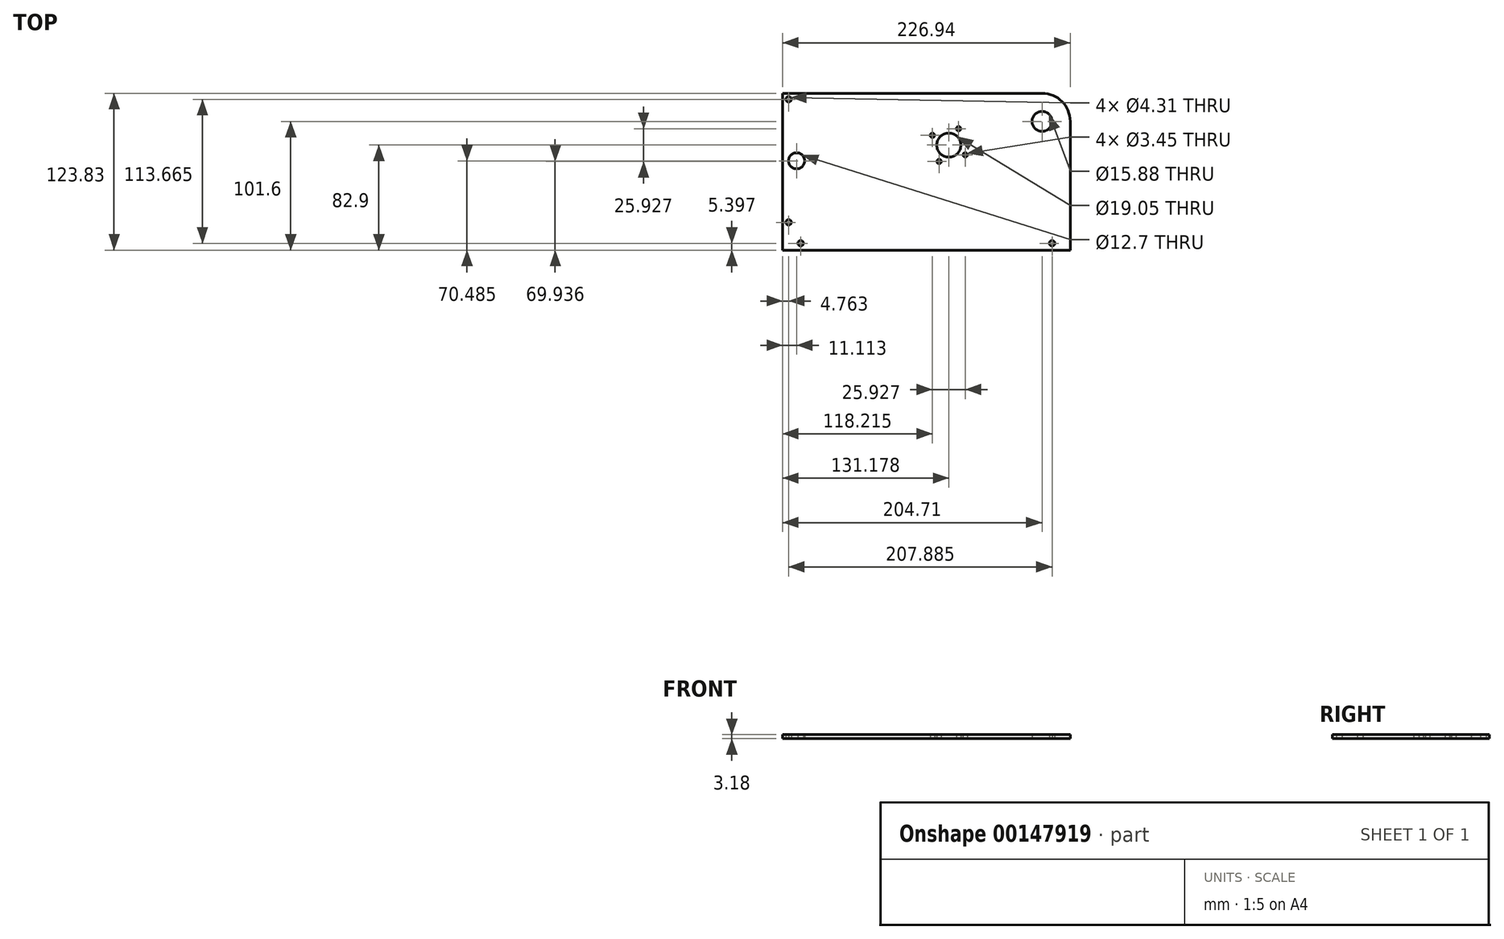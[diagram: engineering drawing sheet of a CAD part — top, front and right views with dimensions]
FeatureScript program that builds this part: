
annotation { "Feature Type Name" : "Feature", "Feature Type Description" : "" }
export const myFeature = defineFeature(function(context is Context, id is Id, definition is map)
    precondition{}
    {
        {
            var Q0;
            Q0=qCreatedBy(makeId("Top.planeOp"),FACE);
            var sketch = newSketch(context, id + "F0", { "sketchPlane" : qUnion([Q0])});
            skCircle(sketch, "E0", {"center": v(0, 0) * mm, "radius": 7.94 * mm});
            skLineSegment(sketch, "E1.bottom", {"start": v(-204.7, 22.22) * mm, "end": v(0, 22.23) * mm});
            skLineSegment(sketch, "E1.top", {"start": v(-204.7, -101.6) * mm, "end": v(22.23, -101.6) * mm});
            skLineSegment(sketch, "E1.left", {"start": v(-204.7, 22.22) * mm, "end": v(-204.7, -101.6) * mm});
            skArc(sketch, "E2", {"start": v(22.23, 0) * mm, "mid": v(15.72, 15.72) * mm, "end": v(0, 22.23) * mm});
            skLineSegment(sketch, "E3", {"start": v(22.23, -101.6) * mm, "end": v(22.23, -90.8) * mm});
            skLineSegment(sketch, "E4", {"start": v(22.23, -90.8) * mm, "end": v(22.23, 0) * mm});
            skLineSegment(sketch, "E5", {"start": v(0, 0) * mm, "end": v(0, -101.6) * mm, "construction": true});
            skLineSegment(sketch, "E6", {"start": v(22.23, -96.2) * mm, "end": v(7.94, -96.2) * mm, "construction": true});
            skCircle(sketch, "E7", {"center": v(7.94, -96.2) * mm, "radius": 2.15 * mm});
            skLineSegment(sketch, "E8", {"start": v(-199.95, 22.22) * mm, "end": v(-199.95, 17.46) * mm, "construction": true});
            skLineSegment(sketch, "E9", {"start": v(-204.7, -96.2) * mm, "end": v(-190.42, -96.2) * mm, "construction": true});
            skCircle(sketch, "E10", {"center": v(-190.42, -96.2) * mm, "radius": 2.15 * mm});
            skCircle(sketch, "E11", {"center": v(-199.95, 17.46) * mm, "radius": 2.15 * mm});
            skLineSegment(sketch, "E12", {"start": v(-199.95, -79.7) * mm, "end": v(-199.95, 17.46) * mm, "construction": true});
            skLineSegment(sketch, "E13", {"start": v(-199.95, -79.7) * mm, "end": v(-199.95, -96.2) * mm, "construction": true});
            skCircle(sketch, "E14", {"center": v(-199.95, -79.7) * mm, "radius": 2.15 * mm});
            skLineSegment(sketch, "E15", {"start": v(0, 0) * mm, "end": v(-73.53, -18.7) * mm, "construction": true});
            skLineSegment(sketch, "E16.bottom", {"start": v(-86.5, -11) * mm, "end": v(-65.83, -5.74) * mm, "construction": true});
            skLineSegment(sketch, "E16.top", {"start": v(-81.24, -31.66) * mm, "end": v(-60.57, -26.4) * mm, "construction": true});
            skLineSegment(sketch, "E16.left", {"start": v(-86.5, -11) * mm, "end": v(-81.24, -31.66) * mm, "construction": true});
            skLineSegment(sketch, "E16.right", {"start": v(-65.83, -5.74) * mm, "end": v(-60.57, -26.4) * mm, "construction": true});
            skPoint(sketch, "E16.middle", {"position": v(-73.53, -18.7) * mm});
            skCircle(sketch, "E17", {"center": v(-86.5, -11) * mm, "radius": 1.73 * mm});
            skCircle(sketch, "E18", {"center": v(-65.83, -5.74) * mm, "radius": 1.73 * mm});
            skCircle(sketch, "E19", {"center": v(-73.53, -18.7) * mm, "radius": 9.53 * mm});
            skCircle(sketch, "E20", {"center": v(-81.24, -31.66) * mm, "radius": 1.73 * mm});
            skCircle(sketch, "E21", {"center": v(-60.57, -26.4) * mm, "radius": 1.73 * mm});
            skCircle(sketch, "E22", {"center": v(-73.53, -18.7) * mm, "radius": 11.11 * mm, "construction": true});
            skCircle(sketch, "E23", {"center": v(-81.24, -31.66) * mm, "radius": 3.97 * mm, "construction": true});
            skLineSegment(sketch, "E24", {"start": v(-199.95, 17.46) * mm, "end": v(-204.7, 17.46) * mm, "construction": true});
            skLineSegment(sketch, "E25", {"start": v(-199.95, -31.12) * mm, "end": v(-193.6, -31.12) * mm, "construction": true});
            skCircle(sketch, "E26", {"center": v(-193.6, -31.12) * mm, "radius": 6.35 * mm});
            skSolve(sketch);
        }
        {
            var Q0;
            Q0=qSketchRegion(id+"F0",true);
            extrude(context, id + "F1", {"entities" : qUnion([Q0]), "depth" : 3.17 * mm});
        }
    });
